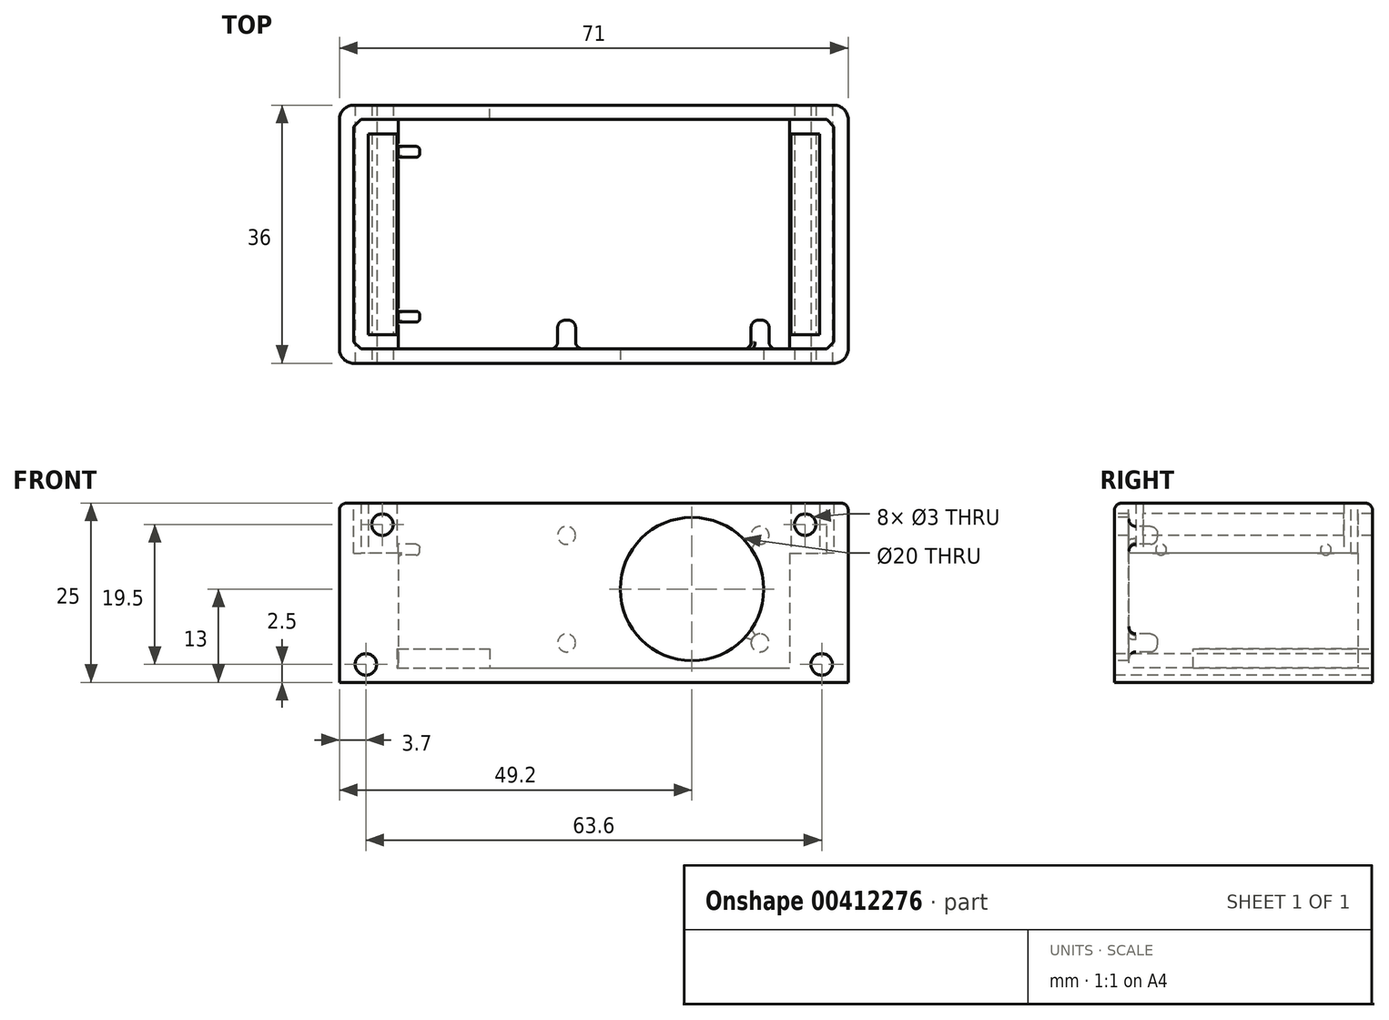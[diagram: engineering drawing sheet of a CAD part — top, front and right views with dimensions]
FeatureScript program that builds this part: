
annotation { "Feature Type Name" : "Feature", "Feature Type Description" : "" }
export const myFeature = defineFeature(function(context is Context, id is Id, definition is map)
    precondition{}
    {
        {
            var Q0;
            Q0=qCreatedBy(makeId("Top.planeOp"),FACE);
            var sketch = newSketch(context, id + "F0", { "sketchPlane" : qUnion([Q0])});
            skLineSegment(sketch, "E0.bottom", {"start": v(0, 0) * mm, "end": v(71, 0) * mm});
            skLineSegment(sketch, "E0.top", {"start": v(0, -36) * mm, "end": v(71, -36) * mm});
            skLineSegment(sketch, "E0.left", {"start": v(0, 0) * mm, "end": v(0, -36) * mm});
            skLineSegment(sketch, "E0.right", {"start": v(71, 0) * mm, "end": v(71, -36) * mm});
            skSolve(sketch);
        }
        {
            var Q0;
            Q0=qSketchRegion(id+"F0",true);
            extrude(context, id + "F1", {"entities" : qUnion([Q0]), "depth" : 2 * mm});
        }
        {
            var Q0;
            Q0=makeQuery(id+"F1.opExtrude","CAP_FACE",FACE,{"disambiguationData":[OSD([sQuery(id+"F0.wireOp",EDGE,"E0.bottom"),sQuery(id+"F0.wireOp",EDGE,"E0.top"),sQuery(id+"F0.wireOp",EDGE,"E0.left"),sQuery(id+"F0.wireOp",EDGE,"E0.right")])],"isStart":false});
            var sketch = newSketch(context, id + "F2", { "sketchPlane" : qUnion([Q0])});
            skLineSegment(sketch, "E1.bottom", {"start": v(2, -2) * mm, "end": v(69, -2) * mm});
            skLineSegment(sketch, "E1.top", {"start": v(2, -34) * mm, "end": v(69, -34) * mm});
            skLineSegment(sketch, "E1.left", {"start": v(2, -2) * mm, "end": v(2, -34) * mm});
            skLineSegment(sketch, "E1.right", {"start": v(69, -2) * mm, "end": v(69, -34) * mm});
            skSolve(sketch);
        }
        {
            var Q0;
            Q0=makeQuery(id+"F2.imprint","IMPRINT",FACE,{"disambiguationData":[TD([[makeQuery(id+"F2.imprint","IMPRINT",EDGE,{"derivedFrom":sQuery(id+"F2.wireOp",EDGE,"E1.bottom")}),1.0]])]});
            extrude(context, id + "F3", {"entities" : qUnion([Q0]), "operationType" : NewBodyOperationType.ADD, "depth" : 23 * mm});
        }
        {
            var Q0;
            Q0=makeQuery(id+"F3.opExtrude","SWEPT_EDGE",EDGE,{"disambiguationData":[OSD([sQuery(id+"F2.wireOp",EDGE,"E1.bottom"),sQuery(id+"F2.wireOp",EDGE,"E1.left")])]});
            var Q1;
            Q1=makeQuery(id+"F3.opExtrude","SWEPT_EDGE",EDGE,{"disambiguationData":[OSD([sQuery(id+"F2.wireOp",EDGE,"E1.top"),sQuery(id+"F2.wireOp",EDGE,"E1.left")])]});
            var Q2;
            Q2=makeQuery(id+"F3.opExtrude","SWEPT_EDGE",EDGE,{"disambiguationData":[OSD([sQuery(id+"F2.wireOp",EDGE,"E1.bottom"),sQuery(id+"F2.wireOp",EDGE,"E1.right")])]});
            var Q3;
            Q3=makeQuery(id+"F3.opExtrude","SWEPT_EDGE",EDGE,{"disambiguationData":[OSD([sQuery(id+"F2.wireOp",EDGE,"E1.top"),sQuery(id+"F2.wireOp",EDGE,"E1.right")])]});
            chamfer(context, id + "F4", {"entities" : qUnion([Q0, Q1, Q2, Q3]), "width" : 1 * mm, "tangentPropagation" : true});
        }
        {
            var Q0;
            {var subQ0=sQuery(id+"F0.wireOp",EDGE,"E0.left");var subQ1=sQuery(id+"F0.wireOp",EDGE,"E0.top");Q0=makeQuery(id+"F3.boolean.opBoolean","MERGE",EDGE,{"derivedFrom":[makeQuery(id+"F1.opExtrude","SWEPT_EDGE",EDGE,{"disambiguationData":[OSD([subQ1,subQ0])]}),makeQuery(id+"F3.opExtrude","SWEPT_EDGE",EDGE,{"disambiguationData":[OSD([subQ1,subQ0])]})]});}
            var Q1;
            {var subQ0=sQuery(id+"F0.wireOp",EDGE,"E0.right");var subQ1=sQuery(id+"F0.wireOp",EDGE,"E0.top");Q1=makeQuery(id+"F3.boolean.opBoolean","MERGE",EDGE,{"derivedFrom":[makeQuery(id+"F1.opExtrude","SWEPT_EDGE",EDGE,{"disambiguationData":[OSD([subQ1,subQ0])]}),makeQuery(id+"F3.opExtrude","SWEPT_EDGE",EDGE,{"disambiguationData":[OSD([subQ1,subQ0])]})]});}
            var Q2;
            {var subQ0=sQuery(id+"F0.wireOp",EDGE,"E0.right");var subQ1=sQuery(id+"F0.wireOp",EDGE,"E0.bottom");Q2=makeQuery(id+"F3.boolean.opBoolean","MERGE",EDGE,{"derivedFrom":[makeQuery(id+"F1.opExtrude","SWEPT_EDGE",EDGE,{"disambiguationData":[OSD([subQ1,subQ0])]}),makeQuery(id+"F3.opExtrude","SWEPT_EDGE",EDGE,{"disambiguationData":[OSD([subQ1,subQ0])]})]});}
            var Q3;
            {var subQ0=sQuery(id+"F0.wireOp",EDGE,"E0.left");var subQ1=sQuery(id+"F0.wireOp",EDGE,"E0.bottom");Q3=makeQuery(id+"F3.boolean.opBoolean","MERGE",EDGE,{"derivedFrom":[makeQuery(id+"F1.opExtrude","SWEPT_EDGE",EDGE,{"disambiguationData":[OSD([subQ1,subQ0])]}),makeQuery(id+"F3.opExtrude","SWEPT_EDGE",EDGE,{"disambiguationData":[OSD([subQ1,subQ0])]})]});}
            fillet(context, id + "F5", {"entities" : qUnion([Q0, Q1, Q2, Q3]), "radius" : 2 * mm, "tangentPropagation" : true, "allowEdgeOverflow" : false});
        }
        {
            var Q0;
            Q0=makeQuery(id+"F3.opExtrude","CAP_EDGE",EDGE,{"disambiguationData":[OSD([sQuery(id+"F0.wireOp",EDGE,"E0.left")])],"isStart":false});
            var Q1;
            Q1=makeQuery(id+"F3.opExtrude","CAP_EDGE",EDGE,{"disambiguationData":[OSD([sQuery(id+"F0.wireOp",EDGE,"E0.top")])],"isStart":false});
            var Q2;
            Q2=makeQuery(id+"F3.opExtrude","CAP_EDGE",EDGE,{"disambiguationData":[OSD([sQuery(id+"F0.wireOp",EDGE,"E0.right")])],"isStart":false});
            var Q3;
            Q3=makeQuery(id+"F3.opExtrude","CAP_EDGE",EDGE,{"disambiguationData":[OSD([sQuery(id+"F0.wireOp",EDGE,"E0.bottom")])],"isStart":false});
            fillet(context, id + "F6", {"entities" : qUnion([Q0, Q1, Q2, Q3]), "radius" : 1 * mm, "tangentPropagation" : true, "allowEdgeOverflow" : false});
        }
        {
            var Q0;
            Q0=makeQuery(id+"F1.opExtrude","CAP_FACE",FACE,{"disambiguationData":[OSD([sQuery(id+"F0.wireOp",EDGE,"E0.bottom"),sQuery(id+"F0.wireOp",EDGE,"E0.top"),sQuery(id+"F0.wireOp",EDGE,"E0.left"),sQuery(id+"F0.wireOp",EDGE,"E0.right")])],"isStart":false});
            var sketch = newSketch(context, id + "F7", { "sketchPlane" : qUnion([Q0])});
            skLineSegment(sketch, "E2.bottom", {"start": v(8.2, -2) * mm, "end": v(2, -2) * mm});
            skLineSegment(sketch, "E2.top", {"start": v(8.2, -34) * mm, "end": v(2, -34) * mm});
            skLineSegment(sketch, "E2.left", {"start": v(8.2, -2) * mm, "end": v(8.2, -34) * mm});
            skLineSegment(sketch, "E2.right", {"start": v(2, -2) * mm, "end": v(2, -34) * mm});
            skLineSegment(sketch, "E3.bottom", {"start": v(62.8, -2) * mm, "end": v(69, -2) * mm});
            skLineSegment(sketch, "E3.top", {"start": v(62.8, -36) * mm, "end": v(69, -36) * mm});
            skLineSegment(sketch, "E3.left", {"start": v(62.8, -2) * mm, "end": v(62.8, -36) * mm});
            skLineSegment(sketch, "E3.right", {"start": v(69, -2) * mm, "end": v(69, -36) * mm});
            skSolve(sketch);
        }
        {
            var Q0;
            Q0=qSketchRegion(id+"F7",true);
            extrude(context, id + "F8", {"entities" : qUnion([Q0]), "operationType" : NewBodyOperationType.ADD, "depth" : 16 * mm});
        }
        {
            var Q0;
            {var subQ0=sQuery(id+"F0.wireOp",EDGE,"E0.top");Q0=makeQuery(id+"F3.boolean.opBoolean","MERGE",FACE,{"derivedFrom":[makeQuery(id+"F1.opExtrude","SWEPT_FACE",FACE,{"disambiguationData":[OSD([subQ0])]}),makeQuery(id+"F3.opExtrude","SWEPT_FACE",FACE,{"disambiguationData":[OSD([subQ0])]})]});}
            var sketch = newSketch(context, id + "F9", { "sketchPlane" : qUnion([Q0])});
            skCircle(sketch, "E4", {"center": v(3.7, 2.5) * mm, "radius": 1.5 * mm});
            skCircle(sketch, "E5", {"center": v(67.3, 2.5) * mm, "radius": 1.5 * mm});
            skSolve(sketch);
        }
        {
            var Q0;
            Q0=qSketchRegion(id+"F9",true);
            extrude(context, id + "F10", {"entities" : qUnion([Q0]), "operationType" : NewBodyOperationType.REMOVE, "endBound" : BoundingType.THROUGH_ALL, "oppositeDirection" : true, "depth" : 25 * mm});
        }
        {
            var Q0;
            Q0=makeQuery(id+"F8.opExtrude","CAP_FACE",FACE,{"disambiguationData":[OSD([sQuery(id+"F7.wireOp",EDGE,"E2.bottom"),sQuery(id+"F7.wireOp",EDGE,"E2.top"),sQuery(id+"F7.wireOp",EDGE,"E2.left"),sQuery(id+"F7.wireOp",EDGE,"E2.right")])],"isStart":false});
            var sketch = newSketch(context, id + "F11", { "sketchPlane" : qUnion([Q0])});
            skLineSegment(sketch, "E6.top", {"start": v(8, -4) * mm, "end": v(4, -4) * mm});
            skLineSegment(sketch, "E6.left", {"start": v(8, -21.2) * mm, "end": v(8, -4) * mm});
            skLineSegment(sketch, "E6.right", {"start": v(4, -21.2) * mm, "end": v(4, -4) * mm});
            skLineSegment(sketch, "E7.top", {"start": v(8, -32) * mm, "end": v(4, -32) * mm});
            skLineSegment(sketch, "E7.left", {"start": v(8, -21.2) * mm, "end": v(8, -32) * mm});
            skLineSegment(sketch, "E7.right", {"start": v(4, -21.2) * mm, "end": v(4, -32) * mm});
            skLineSegment(sketch, "E8.bottom", {"start": v(63, -4) * mm, "end": v(67, -4) * mm});
            skLineSegment(sketch, "E8.left", {"start": v(63, -4) * mm, "end": v(63, -22) * mm});
            skLineSegment(sketch, "E8.right", {"start": v(67, -4) * mm, "end": v(67, -22) * mm});
            skLineSegment(sketch, "E9.top", {"start": v(63, -32) * mm, "end": v(67, -32) * mm});
            skLineSegment(sketch, "E9.left", {"start": v(63, -22) * mm, "end": v(63, -32) * mm});
            skLineSegment(sketch, "E9.right", {"start": v(67, -22) * mm, "end": v(67, -32) * mm});
            skSolve(sketch);
        }
        {
            var Q0;
            Q0=qSketchRegion(id+"F11",true);
            extrude(context, id + "F12", {"entities" : qUnion([Q0]), "operationType" : NewBodyOperationType.ADD, "depth" : 7 * mm});
        }
        {
            var Q0;
            {var subQ0=sQuery(id+"F0.wireOp",EDGE,"E0.top");Q0=makeQuery(id+"F3.boolean.opBoolean","MERGE",FACE,{"derivedFrom":[makeQuery(id+"F1.opExtrude","SWEPT_FACE",FACE,{"disambiguationData":[OSD([subQ0])]}),makeQuery(id+"F3.opExtrude","SWEPT_FACE",FACE,{"disambiguationData":[OSD([subQ0])]})]});}
            var sketch = newSketch(context, id + "F13", { "sketchPlane" : qUnion([Q0])});
            skCircle(sketch, "E10", {"center": v(6, 22) * mm, "radius": 1.5 * mm});
            skCircle(sketch, "E11", {"center": v(65, 22) * mm, "radius": 1.5 * mm});
            skSolve(sketch);
        }
        {
            var Q0;
            Q0=qSketchRegion(id+"F13",true);
            extrude(context, id + "F14", {"entities" : qUnion([Q0]), "operationType" : NewBodyOperationType.REMOVE, "endBound" : BoundingType.THROUGH_ALL, "oppositeDirection" : true, "depth" : 25 * mm});
        }
        {
            var Q0;
            Q0=makeQuery(id+"F1.opExtrude","CAP_FACE",FACE,{"disambiguationData":[OSD([sQuery(id+"F0.wireOp",EDGE,"E0.bottom"),sQuery(id+"F0.wireOp",EDGE,"E0.top"),sQuery(id+"F0.wireOp",EDGE,"E0.left"),sQuery(id+"F0.wireOp",EDGE,"E0.right")])],"isStart":false});
            var sketch = newSketch(context, id + "F15", { "sketchPlane" : qUnion([Q0])});
            skLineSegment(sketch, "E12.bottom", {"start": v(39, -3) * mm, "end": v(62, -3) * mm});
            skLineSegment(sketch, "E12.top", {"start": v(39, -20) * mm, "end": v(62, -20) * mm});
            skLineSegment(sketch, "E12.left", {"start": v(39, -3) * mm, "end": v(39, -20) * mm});
            skLineSegment(sketch, "E12.right", {"start": v(62, -3) * mm, "end": v(62, -20) * mm});
            skSolve(sketch);
        }
        {
            var Q0;
            Q0=makeQuery(id+"F3.opExtrude","SWEPT_FACE",FACE,{"disambiguationData":[OSD([sQuery(id+"F2.wireOp",EDGE,"E1.top")])]});
            var sketch = newSketch(context, id + "F16", { "sketchPlane" : qUnion([Q0])});
            skLineSegment(sketch, "E13.bottom", {"start": v(-29.2, 23) * mm, "end": v(-61.2, 23) * mm});
            skLineSegment(sketch, "E13.top", {"start": v(-29.2, 3) * mm, "end": v(-61.2, 3) * mm});
            skLineSegment(sketch, "E13.left", {"start": v(-29.2, 23) * mm, "end": v(-29.2, 3) * mm});
            skLineSegment(sketch, "E13.right", {"start": v(-61.2, 23) * mm, "end": v(-61.2, 3) * mm});
            skCircle(sketch, "E14", {"center": v(-31.7, 20.5) * mm, "radius": 1.5 * mm});
            skCircle(sketch, "E15", {"center": v(-31.7, 5.5) * mm, "radius": 1.5 * mm});
            skCircle(sketch, "E16", {"center": v(-58.7, 20.5) * mm, "radius": 1.5 * mm});
            skCircle(sketch, "E17", {"center": v(-58.7, 5.5) * mm, "radius": 1.5 * mm});
            skSolve(sketch);
        }
        {
            var Q0;
            {var subQ0=sQuery(id+"F0.wireOp",EDGE,"E0.top");Q0=makeQuery(id+"F3.boolean.opBoolean","MERGE",FACE,{"derivedFrom":[makeQuery(id+"F1.opExtrude","SWEPT_FACE",FACE,{"disambiguationData":[OSD([subQ0])]}),makeQuery(id+"F3.opExtrude","SWEPT_FACE",FACE,{"disambiguationData":[OSD([subQ0])]})]});}
            var sketch = newSketch(context, id + "F17", { "sketchPlane" : qUnion([Q0])});
            skCircle(sketch, "E18", {"center": v(49.2, 13) * mm, "radius": 10 * mm});
            skSolve(sketch);
        }
        {
            var Q0;
            Q0 = qSketchRegion(id + "F17", true);
            var Q1;
            Q1=makeQuery(id+"F3.opExtrude","SWEPT_FACE",FACE,{"disambiguationData":[OSD([sQuery(id+"F2.wireOp",EDGE,"E1.bottom")])]});
            extrude(context, id + "F18", {"entities" : qUnion([Q0]), "operationType" : NewBodyOperationType.REMOVE, "endBound" : BoundingType.UP_TO_SURFACE, "oppositeDirection" : true, "endBoundEntityFace" : qUnion([Q1]), "depth" : 25 * mm});
        }
        {
            var Q0;
            Q0=makeQuery(id+"F16.imprint","IMPRINT",FACE,{"disambiguationData":[TD([[makeQuery(id+"F16.imprint","IMPRINT",EDGE,{"derivedFrom":sQuery(id+"F16.wireOp",EDGE,"E13.bottom")}),1.0]])]});
            var sketch = newSketch(context, id + "F19", { "sketchPlane" : qUnion([Q0])});
            skCircle(sketch, "E19", {"center": v(-58.7, 20.5) * mm, "radius": 1.25 * mm});
            skCircle(sketch, "E20", {"center": v(-31.7, 20.5) * mm, "radius": 1.25 * mm});
            skCircle(sketch, "E21", {"center": v(-31.7, 5.5) * mm, "radius": 1.25 * mm});
            skCircle(sketch, "E22", {"center": v(-58.7, 5.5) * mm, "radius": 1.25 * mm});
            skSolve(sketch);
        }
        {
            var Q0;
            Q0 = qSketchRegion(id + "F19", true);
            extrude(context, id + "F20", {"entities" : qUnion([Q0]), "operationType" : NewBodyOperationType.ADD, "depth" : 4 * mm});
        }
        {
            var Q0;
            Q0=makeQuery(id+"F20.opExtrude","SWEPT_FACE",FACE,{"disambiguationData":[OSD([sQuery(id+"F19.wireOp",EDGE,"E19")])]});
            var Q1;
            Q1=makeQuery(id+"F20.opExtrude","CAP_FACE",FACE,{"disambiguationData":[OSD([sQuery(id+"F19.wireOp",EDGE,"E19")])],"isStart":false});
            var Q2;
            Q2=makeQuery(id+"F20.opExtrude","SWEPT_FACE",FACE,{"disambiguationData":[OSD([sQuery(id+"F19.wireOp",EDGE,"E22")])]});
            var Q3;
            Q3=makeQuery(id+"F20.opExtrude","CAP_FACE",FACE,{"disambiguationData":[OSD([sQuery(id+"F19.wireOp",EDGE,"E22")])],"isStart":false});
            var Q4;
            Q4=makeQuery(id+"F20.opExtrude","SWEPT_FACE",FACE,{"disambiguationData":[OSD([sQuery(id+"F19.wireOp",EDGE,"E20")])]});
            var Q5;
            Q5=makeQuery(id+"F20.opExtrude","CAP_FACE",FACE,{"disambiguationData":[OSD([sQuery(id+"F19.wireOp",EDGE,"E20")])],"isStart":false});
            var Q6;
            Q6=makeQuery(id+"F20.opExtrude","SWEPT_FACE",FACE,{"disambiguationData":[OSD([sQuery(id+"F19.wireOp",EDGE,"E21")])]});
            var Q7;
            Q7=makeQuery(id+"F20.opExtrude","CAP_FACE",FACE,{"disambiguationData":[OSD([sQuery(id+"F19.wireOp",EDGE,"E21")])],"isStart":false});
            fillet(context, id + "F21", {"entities" : qUnion([Q0, Q1, Q2, Q3, Q4, Q5, Q6, Q7]), "radius" : 1 * mm, "tangentPropagation" : true, "allowEdgeOverflow" : false});
        }
        {
            var Q0;
            Q0=makeQuery(id+"F12.boolean.opBoolean","MERGE",FACE,{"derivedFrom":[makeQuery(id+"F8.opExtrude","SWEPT_FACE",FACE,{"disambiguationData":[OSD([sQuery(id+"F7.wireOp",EDGE,"E2.left")])]}),makeQuery(id+"F12.opExtrude","SWEPT_FACE",FACE,{"disambiguationData":[OSD([sQuery(id+"F11.wireOp",EDGE,"E6.left"),sQuery(id+"F11.wireOp",EDGE,"E7.left")])]})]});
            var sketch = newSketch(context, id + "F22", { "sketchPlane" : qUnion([Q0])});
            skLineSegment(sketch, "E23.bottom", {"start": v(-32, 21) * mm, "end": v(-4, 21) * mm});
            skLineSegment(sketch, "E23.top", {"start": v(-32, 4) * mm, "end": v(-4, 4) * mm});
            skLineSegment(sketch, "E23.left", {"start": v(-32, 21) * mm, "end": v(-32, 4) * mm});
            skLineSegment(sketch, "E23.right", {"start": v(-4, 21) * mm, "end": v(-4, 4) * mm});
            skCircle(sketch, "E24", {"center": v(-29.5, 18.5) * mm, "radius": 1 * mm});
            skCircle(sketch, "E25", {"center": v(-6.5, 18.5) * mm, "radius": 1 * mm});
            skSolve(sketch);
        }
        {
            var Q0;
            Q0=makeQuery(id+"F22.imprint","IMPRINT",FACE,{"disambiguationData":[TD([[makeQuery(id+"F22.imprint","IMPRINT",EDGE,{"derivedFrom":sQuery(id+"F22.wireOp",EDGE,"E23.bottom")}),-1.0]])]});
            var sketch = newSketch(context, id + "F23", { "sketchPlane" : qUnion([Q0])});
            skCircle(sketch, "E26", {"center": v(-29.5, 18.5) * mm, "radius": 0.75 * mm});
            skCircle(sketch, "E27", {"center": v(-6.5, 18.5) * mm, "radius": 0.75 * mm});
            skSolve(sketch);
        }
        {
            var Q0;
            Q0 = qSketchRegion(id + "F23", true);
            extrude(context, id + "F24", {"entities" : qUnion([Q0]), "operationType" : NewBodyOperationType.ADD, "depth" : 3 * mm});
        }
        {
            var Q0;
            Q0=makeQuery(id+"F24.opExtrude","SWEPT_FACE",FACE,{"disambiguationData":[OSD([sQuery(id+"F23.wireOp",EDGE,"E26")])]});
            var Q1;
            Q1=makeQuery(id+"F24.opExtrude","CAP_EDGE",EDGE,{"disambiguationData":[OSD([sQuery(id+"F23.wireOp",EDGE,"E26")])],"isStart":false});
            var Q2;
            Q2=makeQuery(id+"F24.opExtrude","SWEPT_FACE",FACE,{"disambiguationData":[OSD([sQuery(id+"F23.wireOp",EDGE,"E27")])]});
            var Q3;
            Q3=makeQuery(id+"F24.opExtrude","CAP_EDGE",EDGE,{"disambiguationData":[OSD([sQuery(id+"F23.wireOp",EDGE,"E27")])],"isStart":false});
            fillet(context, id + "F25", {"entities" : qUnion([Q0, Q1, Q2, Q3]), "radius" : 0.5 * mm, "tangentPropagation" : true, "allowEdgeOverflow" : false});
        }
        {
            var Q0;
            {var subQ0=sQuery(id+"F0.wireOp",EDGE,"E0.bottom");Q0=makeQuery(id+"F3.boolean.opBoolean","MERGE",FACE,{"derivedFrom":[makeQuery(id+"F1.opExtrude","SWEPT_FACE",FACE,{"disambiguationData":[OSD([subQ0])]}),makeQuery(id+"F3.opExtrude","SWEPT_FACE",FACE,{"disambiguationData":[OSD([subQ0])]})]});}
            var sketch = newSketch(context, id + "F26", { "sketchPlane" : qUnion([Q0])});
            skLineSegment(sketch, "E28.bottom", {"start": v(-8, 4.7) * mm, "end": v(-21, 4.7) * mm});
            skLineSegment(sketch, "E28.top", {"start": v(-8, 2) * mm, "end": v(-21, 2) * mm});
            skLineSegment(sketch, "E28.left", {"start": v(-8, 4.7) * mm, "end": v(-8, 2) * mm});
            skLineSegment(sketch, "E28.right", {"start": v(-21, 4.7) * mm, "end": v(-21, 2) * mm});
            skSolve(sketch);
        }
        {
            var Q0;
            Q0 = qSketchRegion(id + "F26", true);
            extrude(context, id + "F27", {"entities" : qUnion([Q0]), "operationType" : NewBodyOperationType.REMOVE, "oppositeDirection" : true, "depth" : 25 * mm});
        }
    });
